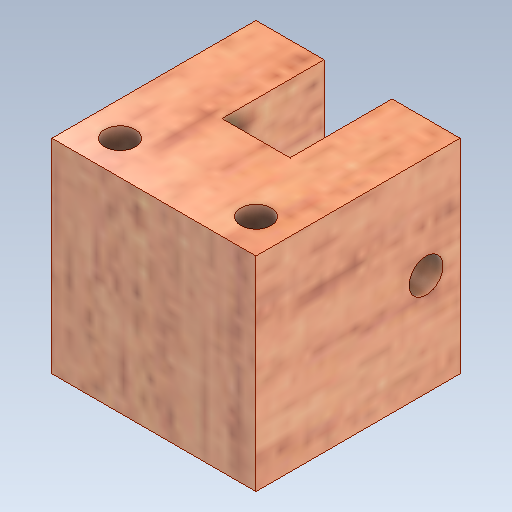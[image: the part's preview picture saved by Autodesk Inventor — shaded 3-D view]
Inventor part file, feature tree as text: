
AUTODESK INVENTOR PART (.ipt)
format: ipt  version: 2020 (Build 240168000, 168)  size: 325,120 bytes
history: native  units: mm
features: sketch x4, extrude x3, hole x1, projected_geometry x1
ambient origin geometry x8: Origin, YZ Plane, XZ Plane, XY Plane, X Axis, Y Axis, Z Axis, Center Point
bodies: Solid1 (feature_tree)
feature tree (9):
  extrude  "Extrusion1"  Depth=30.0mm
  extrude  "Extrusion3"  Depth=10.0mm
  hole  "Hole1"  [1 undecoded]
  extrude  "Extrusion6"  Depth=4.5mm
  sketch  "Sketch1"  dims[d0=30.0mm d1=30.0mm]
  sketch  "Sketch4"  dims[d2=30.0mm d3=0.0mm d8=10.0mm]
  sketch  "Sketch5"  dims[d9=15.0mm d10=0.0mm d11=5.0mm]
  sketch  "Sketch8"  dims[d12=5.0mm d13=6.0mm d14=4.0mm d15=2.0mm d16=90.0deg d17=8.0mm d18=20.594885mm d28=4.5mm d30=5.0mm d31=5.0mm d32=5.0mm d33=0.0mm d34=0.0mm]
  projected_geometry  "Projected Loop1"
note: 1 required parameter value undecoded (feature->parameter linkage not recoverable at this tier; creation-order binding heuristic only, values carry confidence <= 0.55)
